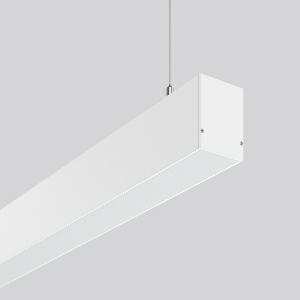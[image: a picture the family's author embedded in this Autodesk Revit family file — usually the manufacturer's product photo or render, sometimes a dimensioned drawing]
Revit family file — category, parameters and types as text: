
# Revit family: less_is_more_50_312315_002_1_76_b58f
name_source: partatom
category: Lighting Fixtures
units: mm (PartAtom-declared; Revit-internal decimal feet)

## family parameters
Cut with Voids When Loaded = No
Host = Face
Light Source = No
Part Type = Normal
Room Calculation Point = No
Round Connector Dimension = Use Diameter
Shared = No

## types (1)
- LESS IS MORE 50 (1 x LED Modul 840, 5650 lm, 4000)
    Apparent Load = 47 VA
    CIE Flux Codes = 48 79 95 100 100
    Color Rendering = 80
    Color Temperature = 4000
    Default Elevation = 1800 mm
    Description = Series: LESS IS MORE 50
Linear pendant luminaire for aesthetically sophisticated lighting. Housing: extruded aluminium profile, powder-coated. End cap aluminium powder-coated. Canopy made of aluminium, powder-coated. Diffuser made of non-yellowing plastic (PMMA), opal. Direct light emission. Suitable for pendant. 2-point steel cable suspension freely positionable and infinitely height-adjustable. Special lengths available on request. LED unit with integrated converter interchangeable and removable. Suitable for through-wiring. With sensors or as a safety luminaire on request. 
Colour: traffic white, matt (RAL 9016)
Length: 1967 mm
Width: 57 mm
Height: 75 mm
Suspension length: 2000 mm
Lamp: LED
Socket: without socket
Colour temperature: 4000K
Colour rendering index (CRI): 80
System power: 47 W
Rated luminous flux: 5650 lm
Luminous efficiency: 120 lm/W
Control gear: Converter, dimmable, DALI
Protection class: I
Type of protection: IP 20
    Height = 75 mm
    Lamp = 1 x LED Modul 840
    Lamp Light Flux = 5650 lm
    Lamp count = 1
    Length = 1967 mm
    Lifetime = 50000 h
    Luminous efficacy = 120 lm/W
    Manufacturer = RZB
    ModVariant = No
    Model = 312315.002.1.76
    Mounting Place = Ceiling
    Mounting Type = Pendant
    Number of Poles = 1
    OnlyDefault = Yes
    Power Factor = 1
    Product Name = LESS IS MORE 50
    Product group = Pendant LED linear luminaires
    ProductGroupID = 907
    Protection Class = Protection class I
    Protection Degree = IP 20
    RLX_Detail_Level = 1
    RLX_Emergency_Light_Flux = 0 lm
    RLX_Emergency_Type = 0
    RLX_Emergency_Type_DB = No
    RlxData = <blob elided: 20601 chars, md5=e69b3acb>
    Socket = socket
    Standby Power = 0 W
    System Light Flux = 5650 lm
    System Power = 47 W
    Type Comments = Product without accessories
    Type Image = 312318.002.jpg
    URL = http://relux.com
    VarID = ---
    Voltage = 230 V
    Voltage Range = 220-240 V
    Weight = 0.00 kg
    Width = 57 mm

## geometry (parser evidence)
native form markers: Blend x4, Sweep x11
no freeform markers — native parametric forms only
